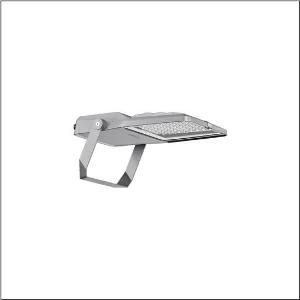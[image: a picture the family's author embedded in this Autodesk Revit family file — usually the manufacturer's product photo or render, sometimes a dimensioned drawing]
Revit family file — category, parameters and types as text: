
# Revit family: floodlight_fl_21_mini___pl52_5xa7776b2d1a_de24
name_source: partatom
category: Lighting Fixtures
units: mm (PartAtom-declared; Revit-internal decimal feet)

## family parameters
Cut with Voids When Loaded = No
Host = Face
Light Source = No
Part Type = Normal
Room Calculation Point = No
Round Connector Dimension = Use Diameter
Shared = No

## types (1)
- --- (1 x LED, 6230 lm, 45.7 W, 3000K)
    Apparent Load = 46 VA
    CIE Flux Codes = 26 60 98 100 100
    Color Rendering = 70
    Color Temperature = 3000K
    Default Elevation = 1800 mm
    Description = Floodlight FL 21 mini, floodlight, primary light control with lens, of PMMA, primary optical cover: protective disc, of toughened safety glass, transparent, light distribution: PL52, light emission: direct distribution, installation type: surface-mounted, LED, High Power LED, rated luminous flux: 6.230lm, luminous efficacy: 136lm/W, light colour: 730, colour temperature: 3000K, control: flexible luminous flux parameterisation, time-dependent luminous flux control, constant luminous flux control, overheat protection, presetting dimming logarithmic, with terminal, 6-pole, mains connection: 220..240V, AC, 50/60Hz, start of lifetime: 46W, end of service life: 48W, reduction: 22W, luminaire housing, of diecast aluminium, powder-coated, Siteco® metallic grey (DB 702S), corrosivity category C5 mid according to DIN EN ISO 12944, sealing non-destructively replaceable, mounting bracket, of steel, galvanised, powder-coated, Siteco® metallic grey (DB 702S), Smart Interface below and above, protection rating (complete): IP66, insulation class (complete): insulation class II (safety insulation), certification: CE, ENEC, VDE, protection symbol: D, impact resistance: IK08, permissible operating ambient temperature: -40..+40°C, permissible operating ambient temperature for outdoor applications: -40..+50°C, standard: DIN EN 12944, LABS conformity tested according to VDMA 24364:2018-05, packaging unit: 1 piece

Light Distribution: PL52
    Height = 70 mm
    Lamp = 1 x LED
    Lamp Light Flux = 6230 lm
    Lamp Power = 45.7 W
    Lamp count = 1
    Length = 485 mm
    Luminous efficacy = 136 lm/W
    Manufacturer = Siteco
    ModVariant = No
    Model = 5XA7776B2D1A
    Number of Poles = 1
    OnlyDefault = Yes
    Power Factor = 1
    Product Name = Floodlight FL 21 mini | PL52
    Product group = floodlight | pylon annexe
    ProductGroupID = 6200
    Protection Class = Protection class II
    Protection Degree = IP 66
    RLX_Detail_Level = 1
    RLX_Emergency_Light_Flux = 0 lm
    RLX_Emergency_Type = 0
    RLX_Emergency_Type_DB = No
    RlxData = <blob elided: 96053 chars, md5=892503ad>
    Socket = socket
    Standby Power = 0 W
    System Light Flux = 6230 lm
    System Power = 46 W
    Type Comments = factory setting: luminous flux: 100 % | dim-lin: 254 | 463 mA
    Type Image = l_1006845.jpg
    URL = http://relux.com
    VarID = @adj_095719
    Voltage = 0 V
    Weight = 0.00 kg
    Width = 337 mm

## geometry (parser evidence)
native form markers: Blend x4, Sweep x12
no freeform markers — native parametric forms only
